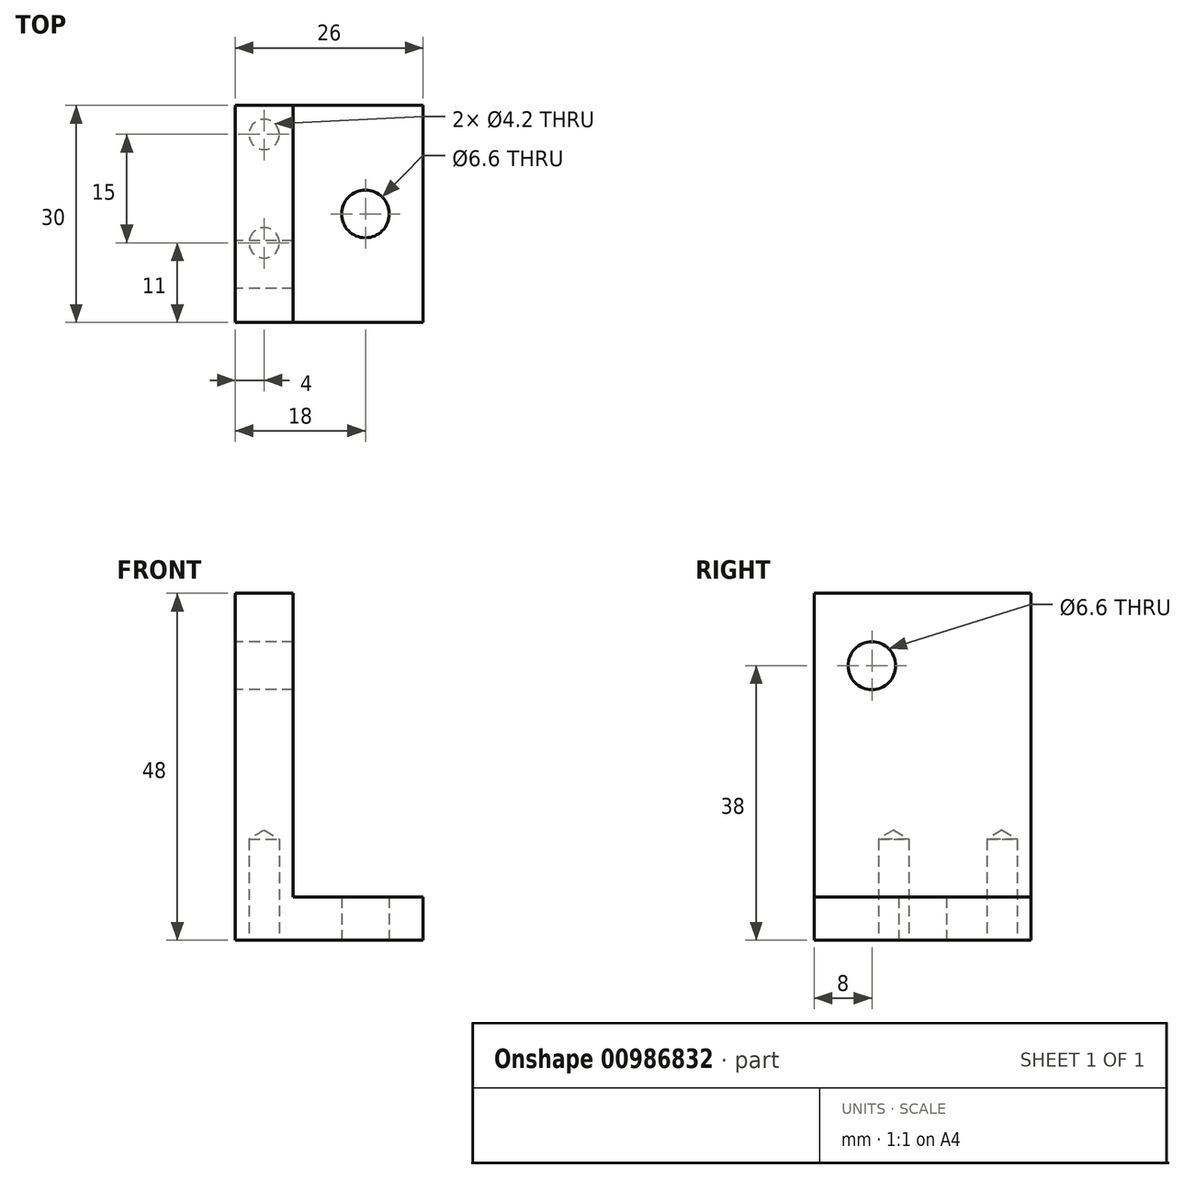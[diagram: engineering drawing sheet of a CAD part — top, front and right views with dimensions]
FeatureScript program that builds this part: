
annotation { "Feature Type Name" : "Feature", "Feature Type Description" : "" }
export const myFeature = defineFeature(function(context is Context, id is Id, definition is map)
    precondition{}
    {
        {
            var Q0;
            Q0=qCreatedBy(makeId("Front.planeOp"),FACE);
            var sketch = newSketch(context, id + "F0", { "sketchPlane" : qUnion([Q0])});
            skLineSegment(sketch, "E0", {"start": v(0, 48) * mm, "end": v(0, 0) * mm});
            skLineSegment(sketch, "E1", {"start": v(0, 0) * mm, "end": v(26, 0) * mm});
            skLineSegment(sketch, "E2", {"start": v(26, 6) * mm, "end": v(26, 0) * mm});
            skLineSegment(sketch, "E3", {"start": v(26, 6) * mm, "end": v(8, 6) * mm});
            skLineSegment(sketch, "E4", {"start": v(8, 6) * mm, "end": v(8, 48) * mm});
            skLineSegment(sketch, "E5", {"start": v(0, 48) * mm, "end": v(8, 48) * mm});
            skSolve(sketch);
        }
        {
            var Q0;
            Q0=makeQuery(id+"F0.imprint","IMPRINT",FACE,{"disambiguationData":[TD([[makeQuery(id+"F0.imprint","IMPRINT",EDGE,{"derivedFrom":sQuery(id+"F0.wireOp",EDGE,"E0")}),1.0]])]});
            extrude(context, id + "F1", {"entities" : qUnion([Q0]), "depth" : 30 * mm, "offsetDistance" : 25 * mm});
        }
        {
            var Q0;
            Q0=makeQuery(id+"F1.opExtrude","SWEPT_FACE",FACE,{"disambiguationData":[OSD([sQuery(id+"F0.wireOp",EDGE,"E0")])]});
            var sketch = newSketch(context, id + "F2", { "sketchPlane" : qUnion([Q0])});
            skPoint(sketch, "E6", {"position": v(22, 38) * mm});
            skSolve(sketch);
        }
        {
            var Q0;
            Q0=sQuery(id+"F2.wireOp",VERTEX,"E6");
            var Q1;
            Q1=makeQuery(id+"F1.opExtrude","SWEPT_BODY",BODY,{"disambiguationData":[OSD([sQuery(id+"F0.wireOp",EDGE,"E0"),sQuery(id+"F0.wireOp",EDGE,"E1"),sQuery(id+"F0.wireOp",EDGE,"E2"),sQuery(id+"F0.wireOp",EDGE,"E3"),sQuery(id+"F0.wireOp",EDGE,"E4"),sQuery(id+"F0.wireOp",EDGE,"E5")])]});
            hole(context, id + "F3", {"style" : HoleStyle.SIMPLE, "endStyle" : HoleEndStyle.THROUGH, "standardTappedOrClearance" : lookupTablePath({ "fit" : "Normal", "standard" : "ISO", "size" : "M6", "type" : "Clearance" }), "standardBlindInLast" : lookupTablePath({ "fit" : "Normal", "standard" : "ISO", "engagement" : "75%", "pitch" : "1 mm", "size" : "M6", "type" : "Clearance & tapped" }), "holeDiameter" : 6.6 * mm, "majorDiameter" : 5 * mm, "isTappedThrough" : true, "tappedDepth" : 7.9 * mm, "tapClearance" : 3, "startFromSketch" : true, "locations" : qUnion([Q0]), "scope" : qUnion([Q1])});
        }
        {
            var Q0;
            Q0=makeQuery(id+"F1.opExtrude","SWEPT_FACE",FACE,{"disambiguationData":[OSD([sQuery(id+"F0.wireOp",EDGE,"E1")])]});
            var sketch = newSketch(context, id + "F4", { "sketchPlane" : qUnion([Q0])});
            skPoint(sketch, "E7", {"position": v(4, 19) * mm});
            skPoint(sketch, "E8", {"position": v(4, 4) * mm});
            skPoint(sketch, "E9", {"position": v(18, 15) * mm});
            skPoint(sketch, "E9.positionSnap0", {"position": v(26, 15) * mm});
            skSolve(sketch);
        }
        {
            var Q0;
            Q0=sQuery(id+"F4.wireOp",VERTEX,"E9");
            var Q1;
            Q1=makeQuery(id+"F1.opExtrude","SWEPT_BODY",BODY,{"disambiguationData":[OSD([sQuery(id+"F0.wireOp",EDGE,"E0"),sQuery(id+"F0.wireOp",EDGE,"E1"),sQuery(id+"F0.wireOp",EDGE,"E2"),sQuery(id+"F0.wireOp",EDGE,"E3"),sQuery(id+"F0.wireOp",EDGE,"E4"),sQuery(id+"F0.wireOp",EDGE,"E5")])]});
            hole(context, id + "F5", {"style" : HoleStyle.SIMPLE, "endStyle" : HoleEndStyle.THROUGH, "standardTappedOrClearance" : lookupTablePath({ "fit" : "Normal", "standard" : "ISO", "size" : "M6", "type" : "Clearance" }), "standardBlindInLast" : lookupTablePath({ "fit" : "Normal", "standard" : "ISO", "engagement" : "75%", "pitch" : "1 mm", "size" : "M6", "type" : "Clearance & tapped" }), "holeDiameter" : 6.6 * mm, "majorDiameter" : 5 * mm, "isTappedThrough" : true, "tappedDepth" : 7.9 * mm, "tapClearance" : 3, "startFromSketch" : true, "locations" : qUnion([Q0]), "scope" : qUnion([Q1])});
        }
        {
            var Q0;
            Q0=sQuery(id+"F4.wireOp",VERTEX,"E8");
            var Q1;
            Q1=sQuery(id+"F4.wireOp",VERTEX,"E7");
            var Q2;
            Q2=makeQuery(id+"F1.opExtrude","SWEPT_BODY",BODY,{"disambiguationData":[OSD([sQuery(id+"F0.wireOp",EDGE,"E0"),sQuery(id+"F0.wireOp",EDGE,"E1"),sQuery(id+"F0.wireOp",EDGE,"E2"),sQuery(id+"F0.wireOp",EDGE,"E3"),sQuery(id+"F0.wireOp",EDGE,"E4"),sQuery(id+"F0.wireOp",EDGE,"E5")])]});
            hole(context, id + "F6", {"style" : HoleStyle.SIMPLE, "endStyle" : HoleEndStyle.BLIND, "standardTappedOrClearance" : lookupTablePath({ "standard" : "ISO", "engagement" : "75%", "pitch" : "0.8 mm", "size" : "M5", "type" : "Tapped" }), "standardBlindInLast" : lookupTablePath({ "standard" : "ISO", "fit" : "Normal", "engagement" : "75%", "pitch" : "0.8 mm", "size" : "M5", "type" : "Clearance & tapped" }), "holeDiameter" : 4.2 * mm, "majorDiameter" : 5 * mm, "showTappedDepth" : true, "holeDepth" : 14 * mm, "isTappedThrough" : true, "tappedDepth" : 11.6 * mm, "tapClearance" : 3, "startFromSketch" : true, "locations" : qUnion([Q0, Q1]), "scope" : qUnion([Q2])});
        }
    });
